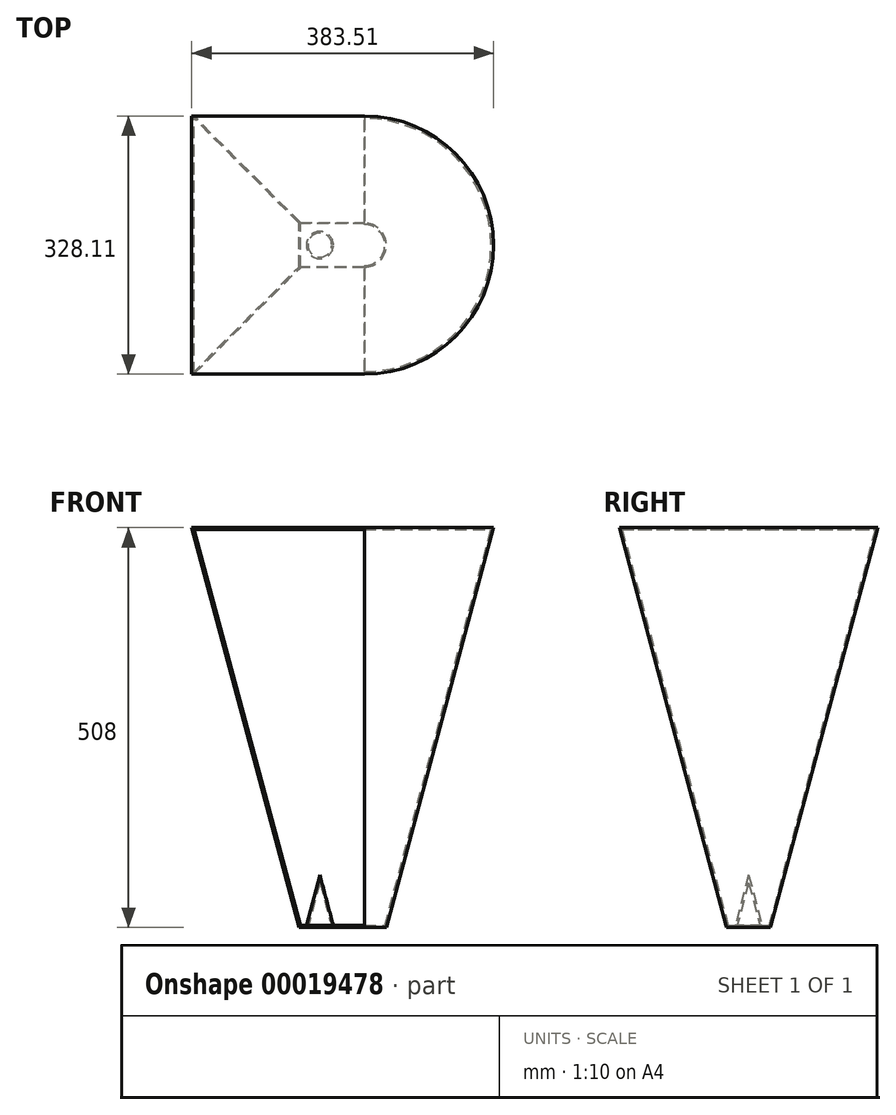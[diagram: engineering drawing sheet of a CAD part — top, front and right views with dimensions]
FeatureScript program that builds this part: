
annotation { "Feature Type Name" : "Feature", "Feature Type Description" : "" }
export const myFeature = defineFeature(function(context is Context, id is Id, definition is map)
    precondition{}
    {
        {
            var Q0;
            Q0=qCreatedBy(makeId("Top.planeOp"),FACE);
            var sketch = newSketch(context, id + "F0", { "sketchPlane" : qUnion([Q0])});
            skLineSegment(sketch, "E0.bottom", {"start": v(-84.02, 64.27) * mm, "end": v(-0.69, 64.27) * mm});
            skLineSegment(sketch, "E0.top", {"start": v(-84.02, 8.4) * mm, "end": v(-0.69, 8.4) * mm});
            skLineSegment(sketch, "E0.left", {"start": v(-84.02, 64.27) * mm, "end": v(-84.02, 8.4) * mm});
            skLineSegment(sketch, "E0.right", {"start": v(-0.69, 64.27) * mm, "end": v(-0.69, 8.4) * mm, "construction": true});
            skArc(sketch, "E1", {"start": v(-0.69, 8.4) * mm, "mid": v(27.25, 36.33) * mm, "end": v(-0.69, 64.27) * mm});
            skCircle(sketch, "E2", {"center": v(-57.28, 36.33) * mm, "radius": 15.24 * mm});
            skLineSegment(sketch, "E3", {"start": v(-84.02, 36.33) * mm, "end": v(-0.69, 36.33) * mm, "construction": true});
            skSolve(sketch);
        }
        {
            var Q0;
            Q0 = qSketchRegion(id + "F0", true);
            extrude(context, id + "F1", {"entities" : qUnion([Q0]), "depth" : 508 * mm, "hasDraft" : true, "draftAngle" : 15 * degree});
        }
        {
            var Q0;
            Q0=makeQuery(id+"F1.opExtrude","SWEPT_FACE",FACE,{"disambiguationData":[OSD([sQuery(id+"F0.wireOp",EDGE,"E0.bottom")])]});
            var Q1;
            Q1=makeQuery(id+"F1.opExtrude","SWEPT_FACE",FACE,{"disambiguationData":[OSD([sQuery(id+"F0.wireOp",EDGE,"E0.top")])]});
            shell(context, id + "F2", {"entities" : qUnion([Q0, Q1]), "thickness" : 2.54 * mm});
        }
    });
